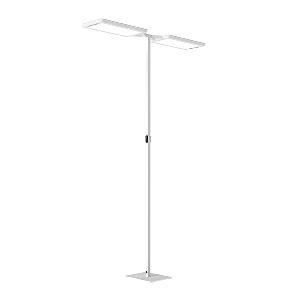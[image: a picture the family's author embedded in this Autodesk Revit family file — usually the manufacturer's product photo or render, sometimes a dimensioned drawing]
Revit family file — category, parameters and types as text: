
# Revit family: yara_doublet_-_yts_2_15000_840_rx_ws_cee_s0_c_114268000-00808399_e0e5
name_source: partatom
category: Lighting Fixtures
units: mm (PartAtom-declared; Revit-internal decimal feet)

## family parameters
Cut with Voids When Loaded = No
Host = Face
Light Source = No
Part Type = Normal
Room Calculation Point = No
Round Connector Dimension = Use Diameter
Shared = No

## types (1)
- YARA.doubleT - YTS 2/15000/840/RX/WS/CEE/S0/C (1 x LED, 15000 lm, 4000K)
    Apparent Load = 214 VA
    Approval mark = CE
    CIE Flux Codes = 58 87 97 13 100
    Color Rendering = 80-89
    Color Temperature = 4000K
    Control Gear = Electronic ballast
    Default Elevation = 1800 mm
    Description = YTS 2/15000/840/RX/WS/CEE/S0/R|Free-standing luminaire|light source: LED|work equipment: Electronic ballast DALI|connected load: 220-240 V, 50/60 Hz|Power consumption: approx. 210 W|power factor: approx. 0,966|luminous flux: 30000 lm|luminous efficacy: 142 lm/W|light distribution: Direct/indirect|direct ratio: approx. 13 %|colour temperature: Cold white, ca. 4000 K|color rendering index (CRI): >= 80|chromaticity tolerance:  3 SDCM|technology: Multiple daylight-dependent motion sensors|operation: Wireless switch|luminaire body|material: Aluminium/plastic|surface: Powder coatet|colour: White|lamp cover: Acrylic (PMMA), Satine, Structured|tubular section|material: Steel tube|surface: Powder-coated|Form: Tubular section upright|colour of tubular section: White|luminaire base|Form: Rectangular flat|weight (net): approx. 24.0 kg|mains lead: 3.00 m Mains plug CEE 7/VII|Fastening: Floor standing base|glare control: Conical prismatic screen|luminance(L65): <= 2700 cd/m|unified glare rating(4H 8H): <=  16|special features: App control, Asymmetric radiation, Direct and indirect lighting component with edge light and light guidetechnology for a homogeneous light exit, Flicker-free, LTX multisensor for workplace optimisation, Magnetic control panel, freely positionable, Optional LTX Cloud connection, TALK Bluetooth|Approval mark: VDE - ENEC|
    Frequency = 50 Hz, 60 Hz
    Height = 24 mm  [stored 0.0787402 ft]
    Lamp = 1 x LED
    Lamp Light Flux = 15000 lm
    Lamp count = 1
    Length = 690 mm
    Luminous efficacy = 140 lm/W
    Manufacturer = Waldmann
    ModVariant = No
    Model = 114268000-00808399
    Mounting Place = Floor
    Mounting Type = Freestanding
    Number of Poles = 1
    OnlyDefault = Yes
    Power Factor = 1
    Product Name = YARA.doubleT - YTS 2/15000/840/RX/WS/CEE/S0/C
    Product group = Free standing luminaire
    ProductGroupID = 13
    Protection Class = Protection class I
    Protection Degree = IP 20
    RLX_Detail_Level = 1
    RlxData = <blob elided: 63113 chars, md5=f2d471e9>
    Socket = socket
    Standby Power = 0 W
    System Light Flux = 30000 lm
    System Power = 214 W
    Type Comments = Product without accessories
    Type Image = yts-rx-ws-r.jpg
    URL = http://relux.com
    VarID = ---
    Voltage = 230 V
    Voltage Range = 220-240 V
    Weight = 0.00 kg
    Width = 358 mm

note: [stored X ft] marks values corroborated as IEEE doubles in the binary element streams (Revit-internal decimal feet)

## geometry (parser evidence)
native form markers: Blend x4, Sweep x19
no freeform markers — native parametric forms only
